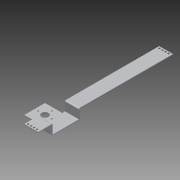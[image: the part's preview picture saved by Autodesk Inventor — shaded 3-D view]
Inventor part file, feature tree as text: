
AUTODESK INVENTOR PART (.ipt)
format: ipt  version: 2013 (Build 170138000, 138)  size: 292,352 bytes
history: native  units: in
note: dims shown in document units (in); Inventor stores cm internally (conversion verified against a paired STEP export)
features: sheet_metal_op x10, reference x8, other x6, sketch x5, projected_geometry x1
ambient origin geometry x8: Origin, YZ Plane, XZ Plane, XY Plane, X Axis, Y Axis, Z Axis, Center Point
bodies: Solid1 (feature_tree)
feature tree (30):
  sheet_metal_op  "Face1"
  sheet_metal_op  "Flange1"
  sheet_metal_op  "Flange2"
  sheet_metal_op  "Flange3"
  sketch  "Sketch1"  dims[d0=1.0in]
  other  "Plate1"
  sketch  "Sketch2"  dims[d1=1.0in]
  other  "Plate2"
  sheet_metal_op  "Bend1"
  sheet_metal_op  "Corner1"
  sketch  "Sketch3"  dims[d2=1.0in]
  other  "Plate3"
  sheet_metal_op  "Bend2"
  sheet_metal_op  "Corner2"
  sketch  "Sketch4"  dims[d3=0.5in]
  other  "Plate4"
  sheet_metal_op  "Bend3"
  sheet_metal_op  "Corner3"
  sketch  "Sketch5"  dims[d4=2.0in d5=2.0in d6=0.5in d7=2.0in d8=0.125in d9=0.125in d10=0.0625in d11=0.25in d12=0.125in d13=1.5in d14=90.0deg d15=0.05in d16=0.5in d17=0.125in d18=0.125in d19=0.125in d20=0.0625in d21=0.25in d22=0.125in d23=2.125in d24=90.0deg d25=0.05in d26=0.5in d27=0.125in d28=0.125in d29=0.125in d30=0.0625in d31=0.25in d32=0.125in d33=13.625in d34=90.0deg d35=0.05in d36=0.5in d37=0.125in d38=0.125in d39=0.125in d40=0.0in]
  projected_geometry  "Projected Loop1"
  reference  "Reference1"
  reference  "Reference2"
  reference  "Reference3"
  reference  "Reference4"
  reference  "Reference5"
  reference  "Reference6"
  reference  "Reference7"
  reference  "Reference8"
  other  "Cut1"
  other  "Definition1"
